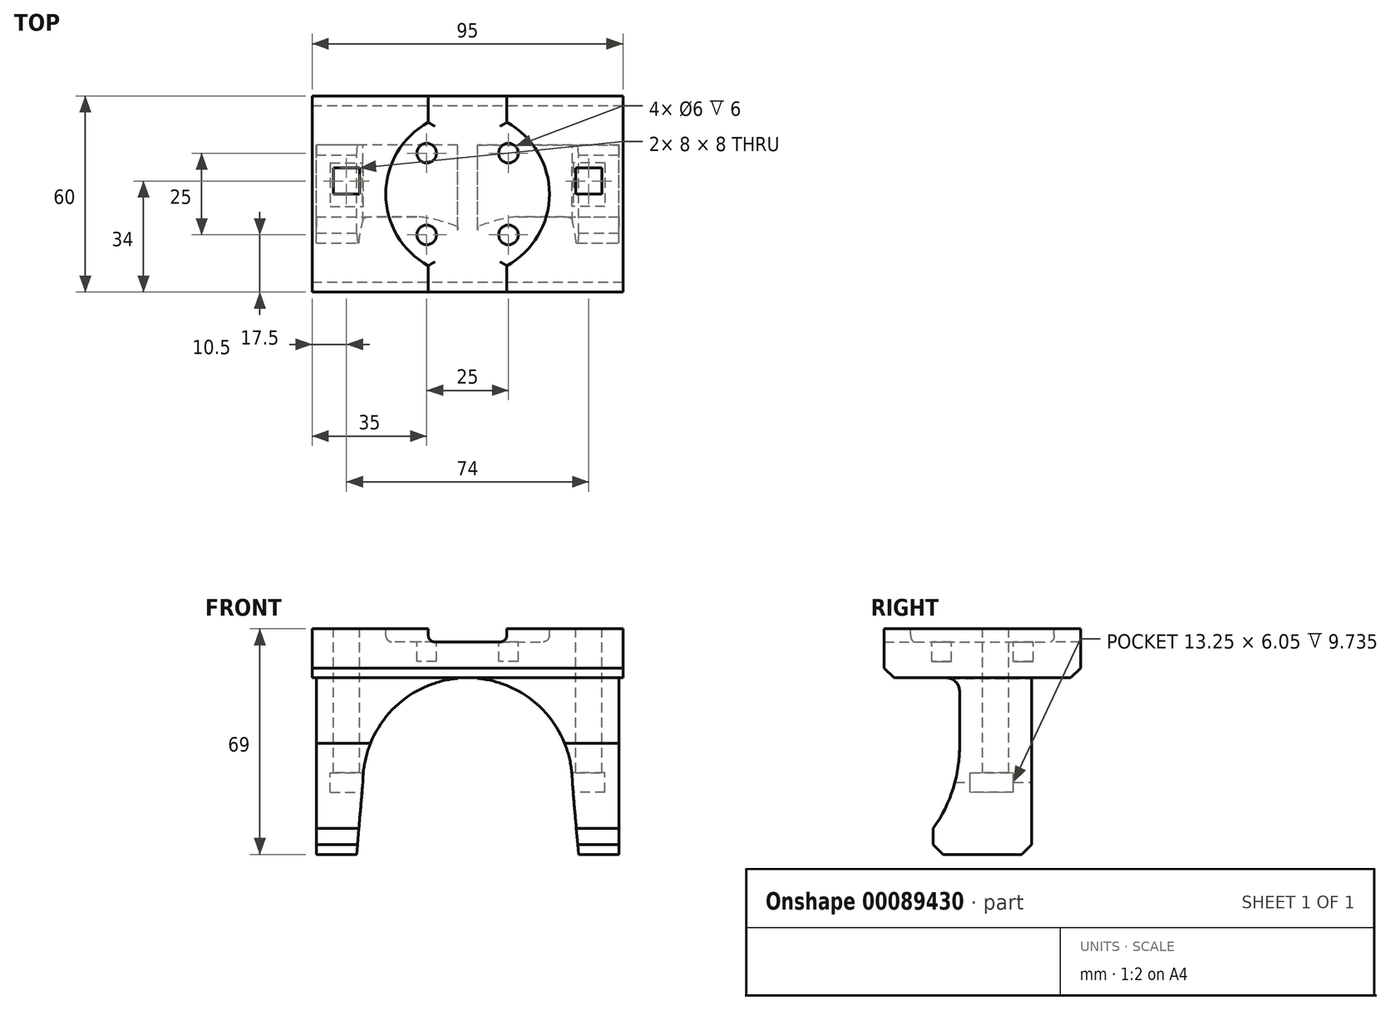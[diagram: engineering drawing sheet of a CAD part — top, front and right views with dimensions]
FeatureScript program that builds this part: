
annotation { "Feature Type Name" : "Feature", "Feature Type Description" : "" }
export const myFeature = defineFeature(function(context is Context, id is Id, definition is map)
    precondition{}
    {
        {
            var Q0;
            Q0=qCreatedBy(makeId("Top.planeOp"),FACE);
            var sketch = newSketch(context, id + "F0", { "sketchPlane" : qUnion([Q0])});
            skLineSegment(sketch, "E0.bottom", {"start": v(47.5, 30) * mm, "end": v(-47.5, 30) * mm});
            skLineSegment(sketch, "E0.top", {"start": v(47.5, -30) * mm, "end": v(-47.5, -30) * mm});
            skLineSegment(sketch, "E0.left", {"start": v(47.5, 30) * mm, "end": v(47.5, -30) * mm});
            skLineSegment(sketch, "E0.right", {"start": v(-47.5, 30) * mm, "end": v(-47.5, -30) * mm});
            skPoint(sketch, "E0.middle", {"position": v(0, 0) * mm});
            skSolve(sketch);
        }
        {
            var Q0;
            Q0=makeQuery(id+"F0.imprint","IMPRINT",FACE,{"disambiguationData":[TD([[makeQuery(id+"F0.imprint","IMPRINT",EDGE,{"derivedFrom":sQuery(id+"F0.wireOp",EDGE,"E0.bottom")}),1.0]])]});
            extrude(context, id + "F1", {"entities" : qUnion([Q0]), "depth" : 15 * mm});
        }
        {
            var Q0;
            Q0=qCreatedBy(makeId("Front.planeOp"),FACE);
            var sketch = newSketch(context, id + "F2", { "sketchPlane" : qUnion([Q0])});
            skLineSegment(sketch, "E1", {"start": v(-46.24, 0) * mm, "end": v(-46.24, -54) * mm});
            skLineSegment(sketch, "E2", {"start": v(-32, -32) * mm, "end": v(-33.92, -54) * mm});
            skLineSegment(sketch, "E3", {"start": v(-33.92, -54) * mm, "end": v(-46.24, -54) * mm});
            skArc(sketch, "E4", {"start": v(-3.07, -0.15) * mm, "mid": v(-23.69, -10.49) * mm, "end": v(-32, -32) * mm});
            skLineSegment(sketch, "E5", {"start": v(-3.08, 0) * mm, "end": v(3.08, 0) * mm, "construction": true});
            skLineSegment(sketch, "E6", {"start": v(-3.08, 0) * mm, "end": v(-3.08, -0.15) * mm});
            skLineSegment(sketch, "E7", {"start": v(-3.07, 0) * mm, "end": v(-46.24, 0) * mm});
            skPoint(sketch, "E8.orphan", {"position": v(0, 0) * mm});
            skArc(sketch, "E9.MirrorCS", {"start": v(3.08, -0.15) * mm, "mid": v(23.69, -10.49) * mm, "end": v(32, -32) * mm});
            skLineSegment(sketch, "E10.MirrorCS", {"start": v(3.08, 0) * mm, "end": v(3.08, -0.15) * mm});
            skLineSegment(sketch, "E11.MirrorCS", {"start": v(3.07, 0) * mm, "end": v(46.24, 0) * mm});
            skLineSegment(sketch, "E12.MirrorCS", {"start": v(46.24, 0) * mm, "end": v(46.24, -54) * mm});
            skLineSegment(sketch, "E13.MirrorCS", {"start": v(33.92, -54) * mm, "end": v(46.24, -54) * mm});
            skLineSegment(sketch, "E14.MirrorCS", {"start": v(32, -32) * mm, "end": v(33.92, -54) * mm});
            skSolve(sketch);
        }
        {
            var Q0;
            Q0=qSketchRegion(id+"F2",true);
            extrude(context, id + "F3", {"entities" : qUnion([Q0]), "operationType" : NewBodyOperationType.ADD, "endBound" : BoundingType.SYMMETRIC, "depth" : 30 * mm});
        }
        {
            var Q0;
            Q0=qCreatedBy(makeId("Right.planeOp"),FACE);
            cPlane(context, id + "F4", {"entities" : qUnion([Q0]), "cplaneType" : CPlaneType.OFFSET, "offset" : 32 * mm, "oppositeDirection" : true, "width" : 150 * mm, "height" : 150 * mm});
        }
        {
            var Q0;
            Q0=qCreatedBy(id+"F4.planeOp",FACE);
            var sketch = newSketch(context, id + "F5", { "sketchPlane" : qUnion([Q0])});
            skLineSegment(sketch, "E15.bottom", {"start": v(9.5, -35.02) * mm, "end": v(-3.75, -35.02) * mm});
            skLineSegment(sketch, "E15.top", {"start": v(9.5, -28.98) * mm, "end": v(-3.75, -28.98) * mm});
            skLineSegment(sketch, "E15.left", {"start": v(9.5, -35.02) * mm, "end": v(9.5, -28.98) * mm});
            skLineSegment(sketch, "E15.right", {"start": v(-3.75, -35.02) * mm, "end": v(-3.75, -28.98) * mm});
            skPoint(sketch, "E15.middle", {"position": v(2.87, -32) * mm});
            skSolve(sketch);
        }
        {
            var Q0;
            Q0 = qSketchRegion(id + "F5", true);
            extrude(context, id + "F6", {"entities" : qUnion([Q0]), "operationType" : NewBodyOperationType.REMOVE, "endBound" : BoundingType.SYMMETRIC, "oppositeDirection" : true, "depth" : 20 * mm});
        }
        {
            var Q0;
            Q0=qCreatedBy(makeId("Top.planeOp"),FACE);
            var sketch = newSketch(context, id + "F7", { "sketchPlane" : qUnion([Q0])});
            skLineSegment(sketch, "E16.bottom", {"start": v(-33, 8) * mm, "end": v(-41, 8) * mm});
            skLineSegment(sketch, "E16.top", {"start": v(-33, 0) * mm, "end": v(-41, 0) * mm});
            skLineSegment(sketch, "E16.left", {"start": v(-33, 8) * mm, "end": v(-33, 0) * mm});
            skLineSegment(sketch, "E16.right", {"start": v(-41, 8) * mm, "end": v(-41, 0) * mm});
            skPoint(sketch, "E16.middle", {"position": v(-37, 4) * mm});
            skSolve(sketch);
        }
        {
            var Q0;
            Q0 = qSketchRegion(id + "F7", true);
            extrude(context, id + "F8", {"entities" : qUnion([Q0]), "operationType" : NewBodyOperationType.REMOVE, "endBound" : BoundingType.SYMMETRIC, "oppositeDirection" : true, "depth" : 58 * mm});
        }
        {
            var Q0;
            Q0=makeQuery(id+"F1.opExtrude","SWEPT_BODY",BODY,{"disambiguationData":[OSD([sQuery(id+"F0.wireOp",EDGE,"E0.bottom"),sQuery(id+"F0.wireOp",EDGE,"E0.top"),sQuery(id+"F0.wireOp",EDGE,"E0.left"),sQuery(id+"F0.wireOp",EDGE,"E0.right"),sQuery(id+"F0.wireOp",EDGE,"zFOQlbL7-HC2t-hPj8-Luxn-h5S0Z57aW7go.bottom"),sQuery(id+"F0.wireOp",EDGE,"zFOQlbL7-HC2t-hPj8-Luxn-h5S0Z57aW7go.top"),sQuery(id+"F0.wireOp",EDGE,"zFOQlbL7-HC2t-hPj8-Luxn-h5S0Z57aW7go.left"),sQuery(id+"F0.wireOp",EDGE,"zFOQlbL7-HC2t-hPj8-Luxn-h5S0Z57aW7go.right"),sQuery(id+"F0.wireOp",EDGE,"JrXA6PBr-tPex-jOhf-22ll-jyP1Bfv6VaY5.bottom"),sQuery(id+"F0.wireOp",EDGE,"JrXA6PBr-tPex-jOhf-22ll-jyP1Bfv6VaY5.top"),sQuery(id+"F0.wireOp",EDGE,"JrXA6PBr-tPex-jOhf-22ll-jyP1Bfv6VaY5.left"),sQuery(id+"F0.wireOp",EDGE,"JrXA6PBr-tPex-jOhf-22ll-jyP1Bfv6VaY5.right")])]});
            var Q1;
            Q1=qCreatedBy(makeId("Right.planeOp"),FACE);
            mirror(context, id + "F9", {"operationType" : NewBodyOperationType.INTERSECT, "entities" : qUnion([Q0]), "mirrorPlane" : qUnion([Q1])});
        }
        {
            var Q0;
            Q0=makeQuery(id+"F3.opExtrude","SWEPT_FACE",FACE,{"disambiguationData":[OSD([sQuery(id+"F2.wireOp",EDGE,"E12.MirrorCS")])]});
            var sketch = newSketch(context, id + "F10", { "sketchPlane" : qUnion([Q0])});
            skLineSegment(sketch, "E17", {"start": v(-7, 0) * mm, "end": v(-7, -20) * mm});
            skLineSegment(sketch, "E18", {"start": v(-15, -46) * mm, "end": v(-15, 0) * mm});
            skLineSegment(sketch, "E19", {"start": v(-15, 0) * mm, "end": v(-7, 0) * mm});
            skArc(sketch, "E20", {"start": v(-15, -46) * mm, "mid": v(-8.89, -33.65) * mm, "end": v(-7, -20) * mm});
            skSolve(sketch);
        }
        {
            var Q0;
            Q0 = qSketchRegion(id + "F10", true);
            extrude(context, id + "F11", {"entities" : qUnion([Q0]), "operationType" : NewBodyOperationType.REMOVE, "oppositeDirection" : true, "depth" : 93 * mm});
        }
        {
            var Q0;
            Q0=makeQuery(id+"F3.opExtrude","CAP_EDGE",EDGE,{"disambiguationData":[OSD([sQuery(id+"F2.wireOp",EDGE,"E13.MirrorCS")])],"isStart":false});
            var Q1;
            Q1=makeQuery(id+"F3.opExtrude","CAP_EDGE",EDGE,{"disambiguationData":[OSD([sQuery(id+"F2.wireOp",EDGE,"E3")])],"isStart":false});
            var Q2;
            Q2=makeQuery(id+"F1.opExtrude","CAP_EDGE",EDGE,{"disambiguationData":[OSD([sQuery(id+"F0.wireOp",EDGE,"E0.top")])],"isStart":true});
            var Q3;
            Q3=makeQuery(id+"F1.opExtrude","CAP_EDGE",EDGE,{"disambiguationData":[OSD([sQuery(id+"F0.wireOp",EDGE,"E0.bottom")])],"isStart":true});
            var Q4;
            Q4=makeQuery(id+"F3.opExtrude","CAP_EDGE",EDGE,{"disambiguationData":[OSD([sQuery(id+"F2.wireOp",EDGE,"E13.MirrorCS")])],"isStart":true});
            var Q5;
            Q5=makeQuery(id+"F3.opExtrude","CAP_EDGE",EDGE,{"disambiguationData":[OSD([sQuery(id+"F2.wireOp",EDGE,"E3")])],"isStart":true});
            chamfer(context, id + "F12", {"entities" : qUnion([Q0, Q1, Q2, Q3, Q4, Q5]), "width" : 3 * mm, "tangentPropagation" : true});
        }
        {
            var Q0;
            Q0=makeQuery(id+"F1.opExtrude","CAP_FACE",FACE,{"disambiguationData":[OSD([sQuery(id+"F0.wireOp",EDGE,"E0.bottom"),sQuery(id+"F0.wireOp",EDGE,"E0.top"),sQuery(id+"F0.wireOp",EDGE,"E0.left"),sQuery(id+"F0.wireOp",EDGE,"E0.right")])],"isStart":false});
            var sketch = newSketch(context, id + "F13", { "sketchPlane" : qUnion([Q0])});
            skCircle(sketch, "E21", {"center": v(0, 0) * mm, "radius": 25 * mm, "construction": true});
            skLineSegment(sketch, "E22", {"start": v(-12, 21.93) * mm, "end": v(-12, 30) * mm});
            skLineSegment(sketch, "E23", {"start": v(-12, 30) * mm, "end": v(12, 30) * mm});
            skLineSegment(sketch, "E24", {"start": v(12, 30) * mm, "end": v(12, 21.93) * mm});
            skLineSegment(sketch, "E25", {"start": v(12, -21.93) * mm, "end": v(12, -30) * mm});
            skLineSegment(sketch, "E26", {"start": v(12, -30) * mm, "end": v(-12, -30) * mm});
            skLineSegment(sketch, "E27", {"start": v(-12, -30) * mm, "end": v(-12, -21.93) * mm});
            skArc(sketch, "E28", {"start": v(-12, 21.93) * mm, "mid": v(-25, 0) * mm, "end": v(-12, -21.93) * mm});
            skArc(sketch, "E29", {"start": v(12, 21.93) * mm, "mid": v(25, 0) * mm, "end": v(12, -21.93) * mm});
            skSolve(sketch);
        }
        {
            var Q0;
            Q0=makeQuery(id+"F13.imprint","IMPRINT",FACE,{"disambiguationData":[TD([[makeQuery(id+"F13.imprint","IMPRINT",EDGE,{"derivedFrom":sQuery(id+"F13.wireOp",EDGE,"E22")}),-1.0]])]});
            extrude(context, id + "F14", {"entities" : qUnion([Q0]), "operationType" : NewBodyOperationType.REMOVE, "oppositeDirection" : true, "depth" : 4 * mm});
        }
        {
            var Q0;
            Q0=makeQuery(id+"F14.boolean.opBoolean","COPY",FACE,{"derivedFrom":makeQuery(id+"F14.opExtrude","CAP_FACE",FACE,{"disambiguationData":[OSD([sQuery(id+"F13.wireOp",EDGE,"E22"),sQuery(id+"F13.wireOp",EDGE,"E23"),sQuery(id+"F13.wireOp",EDGE,"E24"),sQuery(id+"F13.wireOp",EDGE,"E25"),sQuery(id+"F13.wireOp",EDGE,"E26"),sQuery(id+"F13.wireOp",EDGE,"E27"),sQuery(id+"F13.wireOp",EDGE,"E28"),sQuery(id+"F13.wireOp",EDGE,"E29")])],"isStart":false})});
            var sketch = newSketch(context, id + "F15", { "sketchPlane" : qUnion([Q0])});
            skCircle(sketch, "E30", {"center": v(-12.5, 12.5) * mm, "radius": 3 * mm});
            skCircle(sketch, "E31.0.1.0", {"center": v(-12.5, -12.5) * mm, "radius": 3 * mm});
            skCircle(sketch, "E31.1.0.0", {"center": v(12.5, 12.5) * mm, "radius": 3 * mm});
            skCircle(sketch, "E31.1.1.0", {"center": v(12.5, -12.5) * mm, "radius": 3 * mm});
            skLineSegment(sketch, "E31.direction1", {"start": v(-12.5, 12.5) * mm, "end": v(12.5, 12.5) * mm, "construction": true});
            skLineSegment(sketch, "E31.direction2", {"start": v(-12.5, 12.5) * mm, "end": v(-12.5, -12.5) * mm, "construction": true});
            skSolve(sketch);
        }
        {
            var Q0;
            Q0=makeQuery(id+"F15.imprint","IMPRINT",FACE,{"disambiguationData":[TD([[makeQuery(id+"F15.imprint","IMPRINT",EDGE,{"derivedFrom":sQuery(id+"F15.wireOp",EDGE,"E31.1.1.0")}),1.0]])]});
            var Q1;
            Q1=makeQuery(id+"F15.imprint","IMPRINT",FACE,{"disambiguationData":[TD([[makeQuery(id+"F15.imprint","IMPRINT",EDGE,{"derivedFrom":sQuery(id+"F15.wireOp",EDGE,"E31.0.1.0")}),1.0]])]});
            var Q2;
            Q2=makeQuery(id+"F15.imprint","IMPRINT",FACE,{"disambiguationData":[TD([[makeQuery(id+"F15.imprint","IMPRINT",EDGE,{"derivedFrom":sQuery(id+"F15.wireOp",EDGE,"E30")}),1.0]])]});
            var Q3;
            Q3=makeQuery(id+"F15.imprint","IMPRINT",FACE,{"disambiguationData":[TD([[makeQuery(id+"F15.imprint","IMPRINT",EDGE,{"derivedFrom":sQuery(id+"F15.wireOp",EDGE,"E31.1.0.0")}),1.0]])]});
            var Q4;
            Q4=sQuery(id+"F15.wireOp",EDGE,"E30");
            var Q5;
            Q5=sQuery(id+"F15.wireOp",EDGE,"E31.1.0.0");
            var Q6;
            Q6=sQuery(id+"F15.wireOp",EDGE,"E31.1.1.0");
            var Q7;
            Q7=sQuery(id+"F15.wireOp",EDGE,"E31.0.1.0");
            extrude(context, id + "F16", {"entities" : qUnion([Q0, Q1, Q2, Q3]), "operationType" : NewBodyOperationType.REMOVE, "surfaceEntities" : qUnion([Q4, Q5, Q6, Q7]), "oppositeDirection" : true, "depth" : 6 * mm});
        }
        {
            var Q0;
            Q0=makeQuery(id+"F16.opExtrude","CAP_EDGE",EDGE,{"disambiguationData":[OSD([sQuery(id+"F15.wireOp",EDGE,"E30")])],"isStart":true});
            var Q1;
            Q1=makeQuery(id+"F16.opExtrude","CAP_EDGE",EDGE,{"disambiguationData":[OSD([sQuery(id+"F15.wireOp",EDGE,"E31.1.0.0")])],"isStart":true});
            var Q2;
            Q2=makeQuery(id+"F16.opExtrude","CAP_EDGE",EDGE,{"disambiguationData":[OSD([sQuery(id+"F15.wireOp",EDGE,"E31.1.1.0")])],"isStart":true});
            var Q3;
            Q3=makeQuery(id+"F16.opExtrude","CAP_EDGE",EDGE,{"disambiguationData":[OSD([sQuery(id+"F15.wireOp",EDGE,"E31.0.1.0")])],"isStart":true});
            var Q4;
            Q4=makeQuery(id+"F14.boolean.opBoolean","COPY",EDGE,{"derivedFrom":makeQuery(id+"F14.opExtrude","CAP_EDGE",EDGE,{"disambiguationData":[OSD([sQuery(id+"F13.wireOp",EDGE,"E28")])],"isStart":false})});
            var Q5;
            Q5=makeQuery(id+"F14.boolean.opBoolean","COPY",EDGE,{"derivedFrom":makeQuery(id+"F14.opExtrude","CAP_EDGE",EDGE,{"disambiguationData":[OSD([sQuery(id+"F13.wireOp",EDGE,"E29")])],"isStart":false})});
            var Q6;
            Q6=makeQuery(id+"F14.boolean.opBoolean","COPY",EDGE,{"derivedFrom":makeQuery(id+"F14.opExtrude","CAP_EDGE",EDGE,{"disambiguationData":[OSD([sQuery(id+"F13.wireOp",EDGE,"E27")])],"isStart":false})});
            var Q7;
            Q7=makeQuery(id+"F14.boolean.opBoolean","COPY",EDGE,{"derivedFrom":makeQuery(id+"F14.opExtrude","CAP_EDGE",EDGE,{"disambiguationData":[OSD([sQuery(id+"F13.wireOp",EDGE,"E25")])],"isStart":false})});
            var Q8;
            Q8=makeQuery(id+"F14.boolean.opBoolean","COPY",EDGE,{"derivedFrom":makeQuery(id+"F14.opExtrude","CAP_EDGE",EDGE,{"disambiguationData":[OSD([sQuery(id+"F13.wireOp",EDGE,"E24")])],"isStart":false})});
            var Q9;
            Q9=makeQuery(id+"F14.boolean.opBoolean","COPY",EDGE,{"derivedFrom":makeQuery(id+"F14.opExtrude","CAP_EDGE",EDGE,{"disambiguationData":[OSD([sQuery(id+"F13.wireOp",EDGE,"E22")])],"isStart":false})});
            fillet(context, id + "F17", {"entities" : qUnion([Q0, Q1, Q2, Q3, Q4, Q5, Q6, Q7, Q8, Q9]), "radius" : 2 * mm, "tangentPropagation" : true, "allowEdgeOverflow" : false});
        }
        {
            var Q0;
            Q0=makeQuery(id+"F11.boolean.opBoolean","COPY",EDGE,{"disambiguationData":[OD(1.0)],"derivedFrom":makeQuery(id+"F11.opExtrude","SWEPT_EDGE",EDGE,{"disambiguationData":[OSD([sQuery(id+"F2.wireOp",EDGE,"E11.MirrorCS"),sQuery(id+"F2.wireOp",EDGE,"E12.MirrorCS"),sQuery(id+"F10.wireOp",EDGE,"E17"),sQuery(id+"F10.wireOp",EDGE,"E19")])]})});
            var Q1;
            Q1=makeQuery(id+"F11.boolean.opBoolean","COPY",EDGE,{"disambiguationData":[OD(0.0)],"derivedFrom":makeQuery(id+"F11.opExtrude","SWEPT_EDGE",EDGE,{"disambiguationData":[OSD([sQuery(id+"F2.wireOp",EDGE,"E11.MirrorCS"),sQuery(id+"F2.wireOp",EDGE,"E12.MirrorCS"),sQuery(id+"F10.wireOp",EDGE,"E17"),sQuery(id+"F10.wireOp",EDGE,"E19")])]})});
            var Q2;
            Q2=makeQuery(id+"F3.opExtrude","CAP_EDGE",EDGE,{"disambiguationData":[OSD([sQuery(id+"F2.wireOp",EDGE,"E11.MirrorCS")])],"isStart":true});
            var Q3;
            Q3=makeQuery(id+"F3.opExtrude","CAP_EDGE",EDGE,{"disambiguationData":[OSD([sQuery(id+"F2.wireOp",EDGE,"E7")])],"isStart":true});
            fillet(context, id + "F18", {"entities" : qUnion([Q0, Q1, Q2, Q3]), "radius" : 4 * mm, "tangentPropagation" : true, "allowEdgeOverflow" : false});
        }
    });
